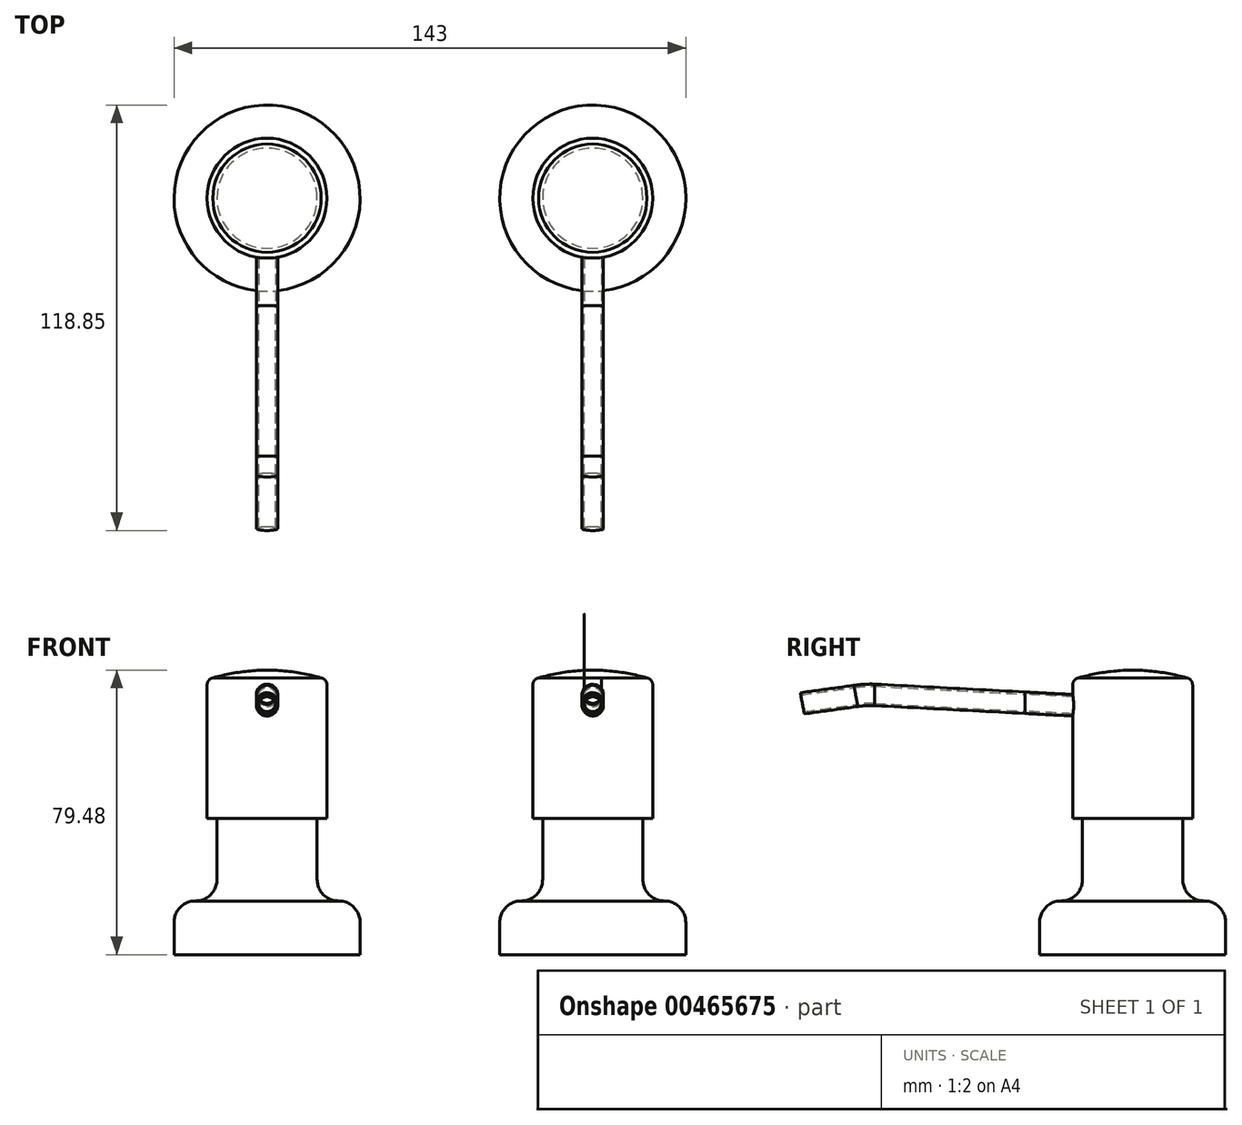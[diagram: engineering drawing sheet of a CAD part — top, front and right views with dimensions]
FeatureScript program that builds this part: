
annotation { "Feature Type Name" : "Feature", "Feature Type Description" : "" }
export const myFeature = defineFeature(function(context is Context, id is Id, definition is map)
    precondition{}
    {
        {
            var Q0;
            Q0=qCreatedBy(makeId("Front.planeOp"),FACE);
            var sketch = newSketch(context, id + "F0", { "sketchPlane" : qUnion([Q0])});
            skLineSegment(sketch, "E0", {"start": v(0, 0) * mm, "end": v(0, 86.2) * mm, "construction": true});
            skLineSegment(sketch, "E1", {"start": v(-26, 0) * mm, "end": v(-26, 9) * mm});
            skArc(sketch, "E2", {"start": v(-20, 15) * mm, "mid": v(-24.24, 13.24) * mm, "end": v(-26, 9) * mm});
            skLineSegment(sketch, "E3", {"start": v(-14, 38) * mm, "end": v(-14, 21) * mm});
            skArc(sketch, "E4", {"start": v(-20, 15) * mm, "mid": v(-15.76, 16.76) * mm, "end": v(-14, 21) * mm});
            skLineSegment(sketch, "E5", {"start": v(-14, 38) * mm, "end": v(-16.75, 38) * mm});
            skLineSegment(sketch, "E6", {"start": v(-16.75, 38) * mm, "end": v(-16.75, 75.36) * mm});
            skLineSegment(sketch, "E7", {"start": v(-26, 0) * mm, "end": v(0, 0) * mm});
            skPoint(sketch, "E8.visualSharp", {"position": v(-16.75, 77) * mm});
            skArc(sketch, "E8.filletArc", {"start": v(-15.14, 77.32) * mm, "mid": v(-16.3, 76.63) * mm, "end": v(-16.75, 75.36) * mm});
            skLineSegment(sketch, "E9", {"start": v(0, 79.48) * mm, "end": v(0, 0) * mm});
            skArc(sketch, "E10", {"start": v(0, 79.48) * mm, "mid": v(-7.64, 78.91) * mm, "end": v(-15.14, 77.32) * mm});
            skSolve(sketch);
        }
        {
            var Q0;
            Q0 = qSketchRegion(id + "F0", true);
            var Q1;
            Q1=sQuery(id+"F0.wireOp",EDGE,"E10");
            var Q2;
            Q2=sQuery(id+"F0.wireOp",EDGE,"E8.filletArc");
            var Q3;
            Q3=sQuery(id+"F0.wireOp",EDGE,"E6");
            var Q4;
            Q4=sQuery(id+"F0.wireOp",EDGE,"E5");
            var Q5;
            Q5=sQuery(id+"F0.wireOp",EDGE,"E3");
            var Q6;
            Q6=sQuery(id+"F0.wireOp",EDGE,"E4");
            var Q7;
            Q7=sQuery(id+"F0.wireOp",EDGE,"E2");
            var Q8;
            Q8=sQuery(id+"F0.wireOp",EDGE,"E7");
            var Q9;
            Q9=sQuery(id+"F0.wireOp",EDGE,"E1");
            var Q10;
            Q10=sQuery(id+"F0.wireOp",EDGE,"E0");
            revolve(context, id + "F1", {"entities" : qUnion([Q0]), "surfaceEntities" : qUnion([Q1, Q2, Q3, Q4, Q5, Q6, Q7, Q8, Q9]), "axis" : qUnion([Q10]), "revolveType" : RevolveType.FULL});
        }
        {
            var Q0;
            Q0=qCreatedBy(makeId("Right.planeOp"),FACE);
            cPlane(context, id + "F2", {"entities" : qUnion([Q0]), "cplaneType" : CPlaneType.OFFSET, "offset" : 45.5 * mm, "width" : 150 * mm, "height" : 150 * mm});
        }
        {
            var Q0;
            Q0=qCreatedBy(makeId("Front.planeOp"),FACE);
            cPlane(context, id + "F3", {"entities" : qUnion([Q0]), "cplaneType" : CPlaneType.OFFSET, "offset" : 30 * mm, "width" : 150 * mm, "height" : 150 * mm});
        }
        {
            var Q0;
            Q0=qCreatedBy(makeId("Right.planeOp"),FACE);
            var sketch = newSketch(context, id + "F4", { "sketchPlane" : qUnion([Q0])});
            skLineSegment(sketch, "E11", {"start": v(-30, 62.32) * mm, "end": v(-72.05, 64.53) * mm});
            skLineSegment(sketch, "E12", {"start": v(-75.8, 64.37) * mm, "end": v(-90.78, 62.32) * mm});
            skPoint(sketch, "E13.visualSharp", {"position": v(-73.94, 64.63) * mm});
            skArc(sketch, "E13.filletArc", {"start": v(-72.05, 64.53) * mm, "mid": v(-73.94, 64.54) * mm, "end": v(-75.8, 64.37) * mm});
            skSolve(sketch);
        }
        {
            var Q0;
            Q0=qCreatedBy(id+"F3.planeOp",FACE);
            var sketch = newSketch(context, id + "F5", { "sketchPlane" : qUnion([Q0])});
            skCircle(sketch, "E14", {"center": v(0, 70.36) * mm, "radius": 3 * mm});
            skCircle(sketch, "E15", {"center": v(0, 70.36) * mm, "radius": 2.38 * mm});
            skSolve(sketch);
        }
        {
            var Q0;
            Q0 = qSketchRegion(id + "F5", true);
            var Q1;
            Q1 = qConstructionFilter(qBodyType(qCreatedBy(id + "F4" ,EDGE), BodyType.WIRE), ConstructionObject.NO);
            sweep(context, id + "F6", {"profiles" : qUnion([Q0]), "path" : qUnion([Q1])});
        }
        {
            var Q0;
            Q0=qCreatedBy(makeId("Right.planeOp"),FACE);
            var sketch = newSketch(context, id + "F7", { "sketchPlane" : qUnion([Q0])});
            skLineSegment(sketch, "E16", {"start": v(0, 60) * mm, "end": v(-29.96, 61.57) * mm});
            skSolve(sketch);
        }
        {
            var Q0;
            Q0 = qSketchRegion(id + "F5", true);
            var Q1;
            Q1 = qConstructionFilter(qBodyType(qCreatedBy(id + "F7" ,EDGE), BodyType.WIRE), ConstructionObject.NO);
            sweep(context, id + "F8", {"operationType" : NewBodyOperationType.ADD, "profiles" : qUnion([Q0]), "path" : qUnion([Q1])});
        }
        {
            var Q0;
            Q0=makeQuery(id+"F1.opRevolve","SWEPT_BODY",BODY,{"disambiguationData":[OSD([sQuery(id+"F0.wireOp",EDGE,"E10")])]});
            var Q1;
            Q1=makeQuery(id+"F6.opSweep","SWEPT_BODY",BODY,{"disambiguationData":[OSD([sQuery(id+"F4.wireOp",EDGE,"E12"),sQuery(id+"F5.wireOp",EDGE,"E14"),sQuery(id+"F5.wireOp",EDGE,"E15")])]});
            var Q2;
            Q2=qCreatedBy(id+"F2.planeOp",FACE);
            mirror(context, id + "F9", {"entities" : qUnion([Q0, Q1]), "mirrorPlane" : qUnion([Q2])});
        }
    });
